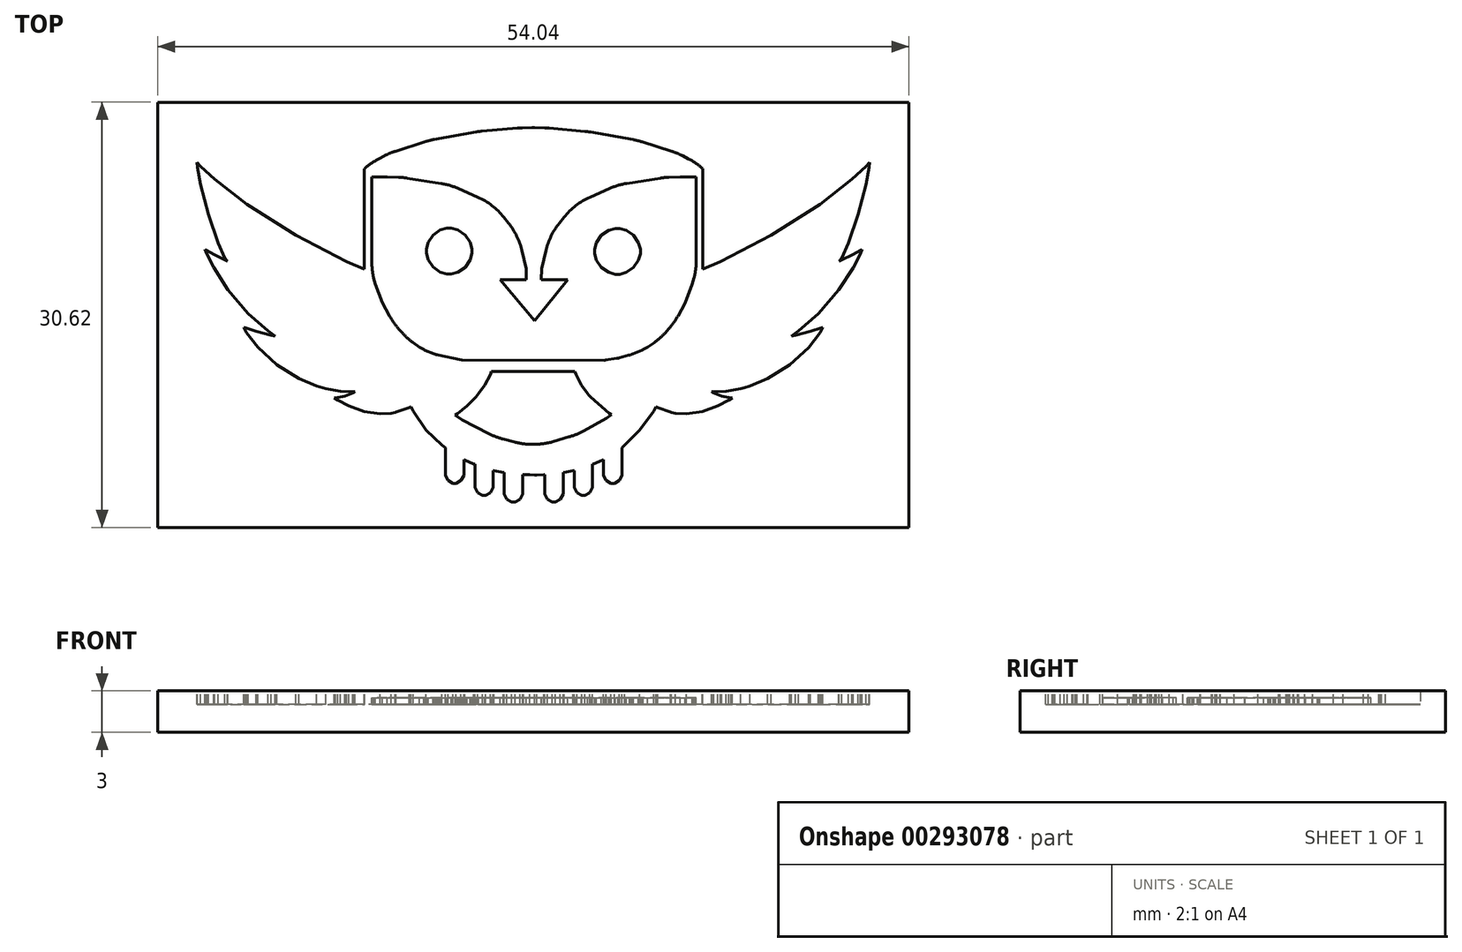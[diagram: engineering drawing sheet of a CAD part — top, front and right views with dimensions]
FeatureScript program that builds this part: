
annotation { "Feature Type Name" : "Feature", "Feature Type Description" : "" }
export const myFeature = defineFeature(function(context is Context, id is Id, definition is map)
    precondition{}
    {
        {
            var Q0;
            Q0=qCreatedBy(makeId("Top.planeOp"),FACE);
            var sketch = newSketch(context, id + "F0", { "sketchPlane" : qUnion([Q0])});
            skLineSegment(sketch, "E0.bottom", {"start": v(27.02, -15.3) * mm, "end": v(-27.02, -15.3) * mm});
            skLineSegment(sketch, "E0.top", {"start": v(27.02, 15.3) * mm, "end": v(-27.02, 15.3) * mm});
            skLineSegment(sketch, "E0.left", {"start": v(27.02, -15.3) * mm, "end": v(27.02, 15.3) * mm});
            skLineSegment(sketch, "E0.right", {"start": v(-27.02, -15.3) * mm, "end": v(-27.02, 15.3) * mm});
            skPoint(sketch, "E0.middle", {"position": v(0, 0) * mm});
            skSolve(sketch);
        }
        {
            var Q0;
            Q0 = qSketchRegion(id + "F0", true);
            extrude(context, id + "F1", {"entities" : qUnion([Q0]), "depth" : 3 * mm});
        }
        {
            var Q0;
            Q0=makeQuery(id+"F1.opExtrude","CAP_FACE",FACE,{"disambiguationData":[OSD([sQuery(id+"F0.wireOp",EDGE,"E0.bottom"),sQuery(id+"F0.wireOp",EDGE,"E0.top"),sQuery(id+"F0.wireOp",EDGE,"E0.left"),sQuery(id+"F0.wireOp",EDGE,"E0.right")])],"isStart":false});
            var sketch = newSketch(context, id + "F2", { "sketchPlane" : qUnion([Q0])});
            skLineSegment(sketch, "E1.bottom", {"start": v(35, -35) * mm, "end": v(-35, -35) * mm});
            skLineSegment(sketch, "E1.top", {"start": v(35, 35) * mm, "end": v(-35, 35) * mm});
            skLineSegment(sketch, "E1.left", {"start": v(35, -35) * mm, "end": v(35, 35) * mm});
            skLineSegment(sketch, "E1.right", {"start": v(-35, -35) * mm, "end": v(-35, 35) * mm});
            skPoint(sketch, "E1.middle", {"position": v(0, 0) * mm});
            skLineSegment(sketch, "E2", {"start": v(18.57, -1.52) * mm, "end": v(18.84, -1.46) * mm});
            skLineSegment(sketch, "E3", {"start": v(18.84, -1.46) * mm, "end": v(19.95, -1.17) * mm});
            skLineSegment(sketch, "E4", {"start": v(19.95, -1.17) * mm, "end": v(20.72, -0.93) * mm});
            skLineSegment(sketch, "E5", {"start": v(20.72, -0.93) * mm, "end": v(20.82, -0.89) * mm});
            skLineSegment(sketch, "E6", {"start": v(20.82, -0.89) * mm, "end": v(20.63, -1.28) * mm});
            skLineSegment(sketch, "E7", {"start": v(20.63, -1.28) * mm, "end": v(19.82, -2.35) * mm});
            skLineSegment(sketch, "E8", {"start": v(19.82, -2.35) * mm, "end": v(18.46, -3.6) * mm});
            skLineSegment(sketch, "E9", {"start": v(18.46, -3.6) * mm, "end": v(16.86, -4.6) * mm});
            skLineSegment(sketch, "E10", {"start": v(16.86, -4.6) * mm, "end": v(15.6, -5.13) * mm});
            skLineSegment(sketch, "E11", {"start": v(15.6, -5.13) * mm, "end": v(15.16, -5.25) * mm});
            skLineSegment(sketch, "E12", {"start": v(15.16, -5.25) * mm, "end": v(14.93, -5.32) * mm});
            skLineSegment(sketch, "E13", {"start": v(14.93, -5.32) * mm, "end": v(13.88, -5.5) * mm});
            skLineSegment(sketch, "E14", {"start": v(13.88, -5.5) * mm, "end": v(12.98, -5.55) * mm});
            skLineSegment(sketch, "E15", {"start": v(12.98, -5.55) * mm, "end": v(12.83, -5.54) * mm});
            skLineSegment(sketch, "E16", {"start": v(12.83, -5.54) * mm, "end": v(12.92, -5.6) * mm});
            skLineSegment(sketch, "E17", {"start": v(12.92, -5.6) * mm, "end": v(13.55, -5.85) * mm});
            skLineSegment(sketch, "E18", {"start": v(13.55, -5.85) * mm, "end": v(14.21, -5.99) * mm});
            skLineSegment(sketch, "E19", {"start": v(14.21, -5.99) * mm, "end": v(14.31, -6) * mm});
            skLineSegment(sketch, "E20", {"start": v(14.31, -6) * mm, "end": v(14.06, -6.15) * mm});
            skLineSegment(sketch, "E21", {"start": v(14.06, -6.15) * mm, "end": v(13.26, -6.56) * mm});
            skLineSegment(sketch, "E22", {"start": v(13.26, -6.56) * mm, "end": v(12.15, -6.97) * mm});
            skLineSegment(sketch, "E23", {"start": v(12.15, -6.97) * mm, "end": v(11.03, -7.14) * mm});
            skLineSegment(sketch, "E24", {"start": v(11.03, -7.14) * mm, "end": v(10.2, -7.1) * mm});
            skLineSegment(sketch, "E25", {"start": v(10.2, -7.1) * mm, "end": v(9.95, -7.02) * mm});
            skLineSegment(sketch, "E26", {"start": v(9.95, -7.02) * mm, "end": v(9.87, -7) * mm});
            skLineSegment(sketch, "E27", {"start": v(9.87, -7) * mm, "end": v(8.94, -6.67) * mm});
            skLineSegment(sketch, "E28", {"start": v(8.94, -6.67) * mm, "end": v(8.84, -6.63) * mm});
            skLineSegment(sketch, "E29", {"start": v(8.84, -6.63) * mm, "end": v(8.66, -6.94) * mm});
            skLineSegment(sketch, "E30", {"start": v(8.66, -6.94) * mm, "end": v(7.64, -8.3) * mm});
            skLineSegment(sketch, "E31", {"start": v(7.64, -8.3) * mm, "end": v(6.57, -9.39) * mm});
            skLineSegment(sketch, "E32", {"start": v(6.57, -9.39) * mm, "end": v(6.38, -9.56) * mm});
            skLineSegment(sketch, "E33", {"start": v(6.38, -9.56) * mm, "end": v(6.38, -11.44) * mm});
            skLineSegment(sketch, "E34", {"start": v(6.38, -11.44) * mm, "end": v(6.38, -11.56) * mm});
            skLineSegment(sketch, "E35", {"start": v(6.38, -11.56) * mm, "end": v(6.18, -11.93) * mm});
            skLineSegment(sketch, "E36", {"start": v(6.18, -11.93) * mm, "end": v(5.83, -12.13) * mm});
            skLineSegment(sketch, "E37", {"start": v(5.83, -12.13) * mm, "end": v(5.71, -12.13) * mm});
            skLineSegment(sketch, "E38", {"start": v(5.71, -12.13) * mm, "end": v(5.6, -12.13) * mm});
            skLineSegment(sketch, "E39", {"start": v(5.6, -12.13) * mm, "end": v(5.24, -11.93) * mm});
            skLineSegment(sketch, "E40", {"start": v(5.24, -11.93) * mm, "end": v(5.05, -11.56) * mm});
            skLineSegment(sketch, "E41", {"start": v(5.05, -11.56) * mm, "end": v(5.05, -11.44) * mm});
            skLineSegment(sketch, "E42", {"start": v(5.05, -11.44) * mm, "end": v(5.05, -10.44) * mm});
            skLineSegment(sketch, "E43", {"start": v(5.05, -10.44) * mm, "end": v(4.99, -10.46) * mm});
            skLineSegment(sketch, "E44", {"start": v(4.99, -10.46) * mm, "end": v(4.33, -10.73) * mm});
            skLineSegment(sketch, "E45", {"start": v(4.33, -10.73) * mm, "end": v(4.26, -10.75) * mm});
            skLineSegment(sketch, "E46", {"start": v(4.26, -10.75) * mm, "end": v(4.26, -12.32) * mm});
            skLineSegment(sketch, "E47", {"start": v(4.26, -12.32) * mm, "end": v(4.26, -12.44) * mm});
            skLineSegment(sketch, "E48", {"start": v(4.26, -12.44) * mm, "end": v(4.07, -12.8) * mm});
            skLineSegment(sketch, "E49", {"start": v(4.07, -12.8) * mm, "end": v(3.71, -13) * mm});
            skLineSegment(sketch, "E50", {"start": v(3.71, -13) * mm, "end": v(3.6, -13) * mm});
            skLineSegment(sketch, "E51", {"start": v(3.6, -13) * mm, "end": v(3.48, -13) * mm});
            skLineSegment(sketch, "E52", {"start": v(3.48, -13) * mm, "end": v(3.13, -12.8) * mm});
            skLineSegment(sketch, "E53", {"start": v(3.13, -12.8) * mm, "end": v(2.94, -12.44) * mm});
            skLineSegment(sketch, "E54", {"start": v(2.94, -12.44) * mm, "end": v(2.94, -12.32) * mm});
            skLineSegment(sketch, "E55", {"start": v(2.94, -12.32) * mm, "end": v(2.94, -11.2) * mm});
            skLineSegment(sketch, "E56", {"start": v(2.94, -11.2) * mm, "end": v(2.87, -11.22) * mm});
            skLineSegment(sketch, "E57", {"start": v(2.87, -11.22) * mm, "end": v(2.2, -11.33) * mm});
            skLineSegment(sketch, "E58", {"start": v(2.2, -11.33) * mm, "end": v(2.14, -11.34) * mm});
            skLineSegment(sketch, "E59", {"start": v(2.14, -11.34) * mm, "end": v(2.14, -12.8) * mm});
            skLineSegment(sketch, "E60", {"start": v(2.14, -12.8) * mm, "end": v(2.14, -12.91) * mm});
            skLineSegment(sketch, "E61", {"start": v(2.14, -12.91) * mm, "end": v(1.95, -13.28) * mm});
            skLineSegment(sketch, "E62", {"start": v(1.95, -13.28) * mm, "end": v(1.6, -13.48) * mm});
            skLineSegment(sketch, "E63", {"start": v(1.6, -13.48) * mm, "end": v(1.48, -13.48) * mm});
            skLineSegment(sketch, "E64", {"start": v(1.48, -13.48) * mm, "end": v(1.36, -13.48) * mm});
            skLineSegment(sketch, "E65", {"start": v(1.36, -13.48) * mm, "end": v(1.01, -13.28) * mm});
            skLineSegment(sketch, "E66", {"start": v(1.01, -13.28) * mm, "end": v(0.82, -12.91) * mm});
            skLineSegment(sketch, "E67", {"start": v(0.82, -12.91) * mm, "end": v(0.82, -12.8) * mm});
            skLineSegment(sketch, "E68", {"start": v(0.82, -12.8) * mm, "end": v(0.82, -11.5) * mm});
            skLineSegment(sketch, "E69", {"start": v(0.82, -11.5) * mm, "end": v(0.75, -11.5) * mm});
            skLineSegment(sketch, "E70", {"start": v(0.75, -11.5) * mm, "end": v(0.25, -11.52) * mm});
            skLineSegment(sketch, "E71", {"start": v(0.25, -11.52) * mm, "end": v(0.08, -11.52) * mm});
            skLineSegment(sketch, "E72", {"start": v(0.08, -11.52) * mm, "end": v(-0.25, -11.52) * mm});
            skLineSegment(sketch, "E73", {"start": v(-0.25, -11.52) * mm, "end": v(-0.7, -11.5) * mm});
            skLineSegment(sketch, "E74", {"start": v(-0.7, -11.5) * mm, "end": v(-0.77, -11.5) * mm});
            skLineSegment(sketch, "E75", {"start": v(-0.77, -11.5) * mm, "end": v(-0.77, -12.8) * mm});
            skLineSegment(sketch, "E76", {"start": v(-0.77, -12.8) * mm, "end": v(-0.77, -12.91) * mm});
            skLineSegment(sketch, "E77", {"start": v(-0.77, -12.91) * mm, "end": v(-0.96, -13.28) * mm});
            skLineSegment(sketch, "E78", {"start": v(-0.96, -13.28) * mm, "end": v(-1.31, -13.48) * mm});
            skLineSegment(sketch, "E79", {"start": v(-1.31, -13.48) * mm, "end": v(-1.43, -13.48) * mm});
            skLineSegment(sketch, "E80", {"start": v(-1.43, -13.48) * mm, "end": v(-1.55, -13.48) * mm});
            skLineSegment(sketch, "E81", {"start": v(-1.55, -13.48) * mm, "end": v(-1.9, -13.28) * mm});
            skLineSegment(sketch, "E82", {"start": v(-1.9, -13.28) * mm, "end": v(-2.1, -12.91) * mm});
            skLineSegment(sketch, "E83", {"start": v(-2.1, -12.91) * mm, "end": v(-2.1, -12.8) * mm});
            skLineSegment(sketch, "E84", {"start": v(-2.1, -12.8) * mm, "end": v(-2.1, -11.34) * mm});
            skLineSegment(sketch, "E85", {"start": v(-2.1, -11.34) * mm, "end": v(-2.16, -11.33) * mm});
            skLineSegment(sketch, "E86", {"start": v(-2.16, -11.33) * mm, "end": v(-2.82, -11.22) * mm});
            skLineSegment(sketch, "E87", {"start": v(-2.82, -11.22) * mm, "end": v(-2.88, -11.2) * mm});
            skLineSegment(sketch, "E88", {"start": v(-2.88, -11.2) * mm, "end": v(-2.88, -12.32) * mm});
            skLineSegment(sketch, "E89", {"start": v(-2.88, -12.32) * mm, "end": v(-2.88, -12.44) * mm});
            skLineSegment(sketch, "E90", {"start": v(-2.88, -12.44) * mm, "end": v(-3.08, -12.8) * mm});
            skLineSegment(sketch, "E91", {"start": v(-3.08, -12.8) * mm, "end": v(-3.43, -13) * mm});
            skLineSegment(sketch, "E92", {"start": v(-3.43, -13) * mm, "end": v(-3.55, -13) * mm});
            skLineSegment(sketch, "E93", {"start": v(-3.55, -13) * mm, "end": v(-3.66, -13) * mm});
            skLineSegment(sketch, "E94", {"start": v(-3.66, -13) * mm, "end": v(-4.02, -12.8) * mm});
            skLineSegment(sketch, "E95", {"start": v(-4.02, -12.8) * mm, "end": v(-4.2, -12.44) * mm});
            skLineSegment(sketch, "E96", {"start": v(-4.2, -12.44) * mm, "end": v(-4.2, -12.32) * mm});
            skLineSegment(sketch, "E97", {"start": v(-4.2, -12.32) * mm, "end": v(-4.2, -10.75) * mm});
            skLineSegment(sketch, "E98", {"start": v(-4.2, -10.75) * mm, "end": v(-4.27, -10.73) * mm});
            skLineSegment(sketch, "E99", {"start": v(-4.27, -10.73) * mm, "end": v(-4.93, -10.47) * mm});
            skLineSegment(sketch, "E100", {"start": v(-4.93, -10.47) * mm, "end": v(-5, -10.44) * mm});
            skLineSegment(sketch, "E101", {"start": v(-5, -10.44) * mm, "end": v(-5, -11.44) * mm});
            skLineSegment(sketch, "E102", {"start": v(-5, -11.44) * mm, "end": v(-5, -11.56) * mm});
            skLineSegment(sketch, "E103", {"start": v(-5, -11.56) * mm, "end": v(-5.2, -11.93) * mm});
            skLineSegment(sketch, "E104", {"start": v(-5.2, -11.93) * mm, "end": v(-5.55, -12.13) * mm});
            skLineSegment(sketch, "E105", {"start": v(-5.55, -12.13) * mm, "end": v(-5.66, -12.13) * mm});
            skLineSegment(sketch, "E106", {"start": v(-5.66, -12.13) * mm, "end": v(-5.78, -12.13) * mm});
            skLineSegment(sketch, "E107", {"start": v(-5.78, -12.13) * mm, "end": v(-6.13, -11.93) * mm});
            skLineSegment(sketch, "E108", {"start": v(-6.13, -11.93) * mm, "end": v(-6.32, -11.56) * mm});
            skLineSegment(sketch, "E109", {"start": v(-6.32, -11.56) * mm, "end": v(-6.32, -11.44) * mm});
            skLineSegment(sketch, "E110", {"start": v(-6.32, -11.44) * mm, "end": v(-6.32, -9.56) * mm});
            skLineSegment(sketch, "E111", {"start": v(-6.32, -9.56) * mm, "end": v(-6.59, -9.39) * mm});
            skLineSegment(sketch, "E112", {"start": v(-6.59, -9.39) * mm, "end": v(-7.7, -8.3) * mm});
            skLineSegment(sketch, "E113", {"start": v(-7.7, -8.3) * mm, "end": v(-8.64, -6.94) * mm});
            skLineSegment(sketch, "E114", {"start": v(-8.64, -6.94) * mm, "end": v(-8.81, -6.63) * mm});
            skLineSegment(sketch, "E115", {"start": v(-8.81, -6.63) * mm, "end": v(-8.92, -6.67) * mm});
            skLineSegment(sketch, "E116", {"start": v(-8.92, -6.67) * mm, "end": v(-9.88, -7) * mm});
            skLineSegment(sketch, "E117", {"start": v(-9.88, -7) * mm, "end": v(-9.95, -7.02) * mm});
            skLineSegment(sketch, "E118", {"start": v(-9.95, -7.02) * mm, "end": v(-10.2, -7.1) * mm});
            skLineSegment(sketch, "E119", {"start": v(-10.2, -7.1) * mm, "end": v(-11.03, -7.14) * mm});
            skLineSegment(sketch, "E120", {"start": v(-11.03, -7.14) * mm, "end": v(-12.15, -6.97) * mm});
            skLineSegment(sketch, "E121", {"start": v(-12.15, -6.97) * mm, "end": v(-13.26, -6.56) * mm});
            skLineSegment(sketch, "E122", {"start": v(-13.26, -6.56) * mm, "end": v(-14.06, -6.15) * mm});
            skLineSegment(sketch, "E123", {"start": v(-14.06, -6.15) * mm, "end": v(-14.31, -6) * mm});
            skLineSegment(sketch, "E124", {"start": v(-14.31, -6) * mm, "end": v(-14.21, -5.99) * mm});
            skLineSegment(sketch, "E125", {"start": v(-14.21, -5.99) * mm, "end": v(-13.55, -5.85) * mm});
            skLineSegment(sketch, "E126", {"start": v(-13.55, -5.85) * mm, "end": v(-12.92, -5.6) * mm});
            skLineSegment(sketch, "E127", {"start": v(-12.92, -5.6) * mm, "end": v(-12.83, -5.54) * mm});
            skLineSegment(sketch, "E128", {"start": v(-12.83, -5.54) * mm, "end": v(-12.99, -5.55) * mm});
            skLineSegment(sketch, "E129", {"start": v(-12.99, -5.55) * mm, "end": v(-13.88, -5.5) * mm});
            skLineSegment(sketch, "E130", {"start": v(-13.88, -5.5) * mm, "end": v(-14.93, -5.32) * mm});
            skLineSegment(sketch, "E131", {"start": v(-14.93, -5.32) * mm, "end": v(-15.16, -5.25) * mm});
            skLineSegment(sketch, "E132", {"start": v(-15.16, -5.25) * mm, "end": v(-15.6, -5.13) * mm});
            skLineSegment(sketch, "E133", {"start": v(-15.6, -5.13) * mm, "end": v(-16.86, -4.59) * mm});
            skLineSegment(sketch, "E134", {"start": v(-16.86, -4.59) * mm, "end": v(-18.46, -3.6) * mm});
            skLineSegment(sketch, "E135", {"start": v(-18.46, -3.6) * mm, "end": v(-19.82, -2.34) * mm});
            skLineSegment(sketch, "E136", {"start": v(-19.82, -2.34) * mm, "end": v(-20.63, -1.28) * mm});
            skLineSegment(sketch, "E137", {"start": v(-20.63, -1.28) * mm, "end": v(-20.82, -0.89) * mm});
            skLineSegment(sketch, "E138", {"start": v(-20.82, -0.89) * mm, "end": v(-20.72, -0.93) * mm});
            skLineSegment(sketch, "E139", {"start": v(-20.72, -0.93) * mm, "end": v(-19.95, -1.17) * mm});
            skLineSegment(sketch, "E140", {"start": v(-19.95, -1.17) * mm, "end": v(-18.85, -1.46) * mm});
            skLineSegment(sketch, "E141", {"start": v(-18.85, -1.46) * mm, "end": v(-18.57, -1.52) * mm});
            skLineSegment(sketch, "E142", {"start": v(-18.57, -1.52) * mm, "end": v(-19.1, -1.17) * mm});
            skLineSegment(sketch, "E143", {"start": v(-19.1, -1.17) * mm, "end": v(-20.52, 0.1) * mm});
            skLineSegment(sketch, "E144", {"start": v(-20.52, 0.1) * mm, "end": v(-21.97, 1.8) * mm});
            skLineSegment(sketch, "E145", {"start": v(-21.97, 1.8) * mm, "end": v(-23, 3.4) * mm});
            skLineSegment(sketch, "E146", {"start": v(-23, 3.4) * mm, "end": v(-23.5, 4.39) * mm});
            skLineSegment(sketch, "E147", {"start": v(-23.5, 4.39) * mm, "end": v(-23.63, 4.72) * mm});
            skLineSegment(sketch, "E148", {"start": v(-23.63, 4.72) * mm, "end": v(-23.54, 4.67) * mm});
            skLineSegment(sketch, "E149", {"start": v(-23.54, 4.67) * mm, "end": v(-22.97, 4.35) * mm});
            skLineSegment(sketch, "E150", {"start": v(-22.97, 4.35) * mm, "end": v(-22.2, 3.96) * mm});
            skLineSegment(sketch, "E151", {"start": v(-22.2, 3.96) * mm, "end": v(-22.01, 3.88) * mm});
            skLineSegment(sketch, "E152", {"start": v(-22.01, 3.88) * mm, "end": v(-22.2, 4.1) * mm});
            skLineSegment(sketch, "E153", {"start": v(-22.2, 4.1) * mm, "end": v(-22.67, 5.16) * mm});
            skLineSegment(sketch, "E154", {"start": v(-22.67, 5.16) * mm, "end": v(-23.38, 7.22) * mm});
            skLineSegment(sketch, "E155", {"start": v(-23.38, 7.22) * mm, "end": v(-23.94, 9.4) * mm});
            skLineSegment(sketch, "E156", {"start": v(-23.94, 9.4) * mm, "end": v(-24.18, 10.62) * mm});
            skLineSegment(sketch, "E157", {"start": v(-24.18, 10.62) * mm, "end": v(-24.18, 10.97) * mm});
            skLineSegment(sketch, "E158", {"start": v(-24.18, 10.97) * mm, "end": v(-23.93, 10.68) * mm});
            skLineSegment(sketch, "E159", {"start": v(-23.93, 10.68) * mm, "end": v(-22.93, 9.75) * mm});
            skLineSegment(sketch, "E160", {"start": v(-22.93, 9.75) * mm, "end": v(-20.62, 7.95) * mm});
            skLineSegment(sketch, "E161", {"start": v(-20.62, 7.95) * mm, "end": v(-17.09, 5.73) * mm});
            skLineSegment(sketch, "E162", {"start": v(-17.09, 5.73) * mm, "end": v(-13.42, 3.84) * mm});
            skLineSegment(sketch, "E163", {"start": v(-13.42, 3.84) * mm, "end": v(-12.17, 3.3) * mm});
            skLineSegment(sketch, "E164", {"start": v(-12.17, 3.3) * mm, "end": v(-12.17, 10.5) * mm});
            skLineSegment(sketch, "E165", {"start": v(-12.17, 10.5) * mm, "end": v(-12.14, 10.5) * mm});
            skLineSegment(sketch, "E166", {"start": v(-12.14, 10.5) * mm, "end": v(-12.14, 10.52) * mm});
            skLineSegment(sketch, "E167", {"start": v(-12.14, 10.52) * mm, "end": v(-11.78, 10.89) * mm});
            skLineSegment(sketch, "E168", {"start": v(-11.78, 10.89) * mm, "end": v(-10.33, 11.65) * mm});
            skLineSegment(sketch, "E169", {"start": v(-10.33, 11.65) * mm, "end": v(-7.47, 12.57) * mm});
            skLineSegment(sketch, "E170", {"start": v(-7.47, 12.57) * mm, "end": v(-3.92, 13.2) * mm});
            skLineSegment(sketch, "E171", {"start": v(-3.92, 13.2) * mm, "end": v(-0.98, 13.46) * mm});
            skLineSegment(sketch, "E172", {"start": v(-0.98, 13.46) * mm, "end": v(0, 13.48) * mm});
            skLineSegment(sketch, "E173", {"start": v(0, 13.48) * mm, "end": v(0.98, 13.46) * mm});
            skLineSegment(sketch, "E174", {"start": v(0.98, 13.46) * mm, "end": v(3.92, 13.19) * mm});
            skLineSegment(sketch, "E175", {"start": v(3.92, 13.19) * mm, "end": v(7.5, 12.55) * mm});
            skLineSegment(sketch, "E176", {"start": v(7.5, 12.55) * mm, "end": v(10.37, 11.64) * mm});
            skLineSegment(sketch, "E177", {"start": v(10.37, 11.64) * mm, "end": v(11.83, 10.89) * mm});
            skLineSegment(sketch, "E178", {"start": v(11.83, 10.89) * mm, "end": v(12.2, 10.52) * mm});
            skLineSegment(sketch, "E179", {"start": v(12.2, 10.52) * mm, "end": v(12.2, 10.46) * mm});
            skLineSegment(sketch, "E180", {"start": v(12.2, 10.46) * mm, "end": v(12.17, 10.46) * mm});
            skLineSegment(sketch, "E181", {"start": v(12.17, 10.46) * mm, "end": v(12.2, 10.46) * mm});
            skLineSegment(sketch, "E182", {"start": v(12.2, 10.46) * mm, "end": v(12.2, 3.3) * mm});
            skLineSegment(sketch, "E183", {"start": v(12.2, 3.3) * mm, "end": v(13.45, 3.84) * mm});
            skLineSegment(sketch, "E184", {"start": v(13.45, 3.84) * mm, "end": v(17.1, 5.73) * mm});
            skLineSegment(sketch, "E185", {"start": v(17.1, 5.73) * mm, "end": v(20.63, 7.95) * mm});
            skLineSegment(sketch, "E186", {"start": v(20.63, 7.95) * mm, "end": v(22.93, 9.75) * mm});
            skLineSegment(sketch, "E187", {"start": v(22.93, 9.75) * mm, "end": v(23.92, 10.68) * mm});
            skLineSegment(sketch, "E188", {"start": v(23.92, 10.68) * mm, "end": v(24.18, 10.97) * mm});
            skLineSegment(sketch, "E189", {"start": v(24.18, 10.97) * mm, "end": v(24.18, 10.62) * mm});
            skLineSegment(sketch, "E190", {"start": v(24.18, 10.62) * mm, "end": v(23.94, 9.4) * mm});
            skLineSegment(sketch, "E191", {"start": v(23.94, 9.4) * mm, "end": v(23.37, 7.23) * mm});
            skLineSegment(sketch, "E192", {"start": v(23.37, 7.23) * mm, "end": v(22.67, 5.16) * mm});
            skLineSegment(sketch, "E193", {"start": v(22.67, 5.16) * mm, "end": v(22.2, 4.1) * mm});
            skLineSegment(sketch, "E194", {"start": v(22.2, 4.1) * mm, "end": v(22.01, 3.88) * mm});
            skLineSegment(sketch, "E195", {"start": v(22.01, 3.88) * mm, "end": v(22.2, 3.96) * mm});
            skLineSegment(sketch, "E196", {"start": v(22.2, 3.96) * mm, "end": v(22.98, 4.35) * mm});
            skLineSegment(sketch, "E197", {"start": v(22.98, 4.35) * mm, "end": v(23.57, 4.67) * mm});
            skLineSegment(sketch, "E198", {"start": v(23.57, 4.67) * mm, "end": v(23.65, 4.72) * mm});
            skLineSegment(sketch, "E199", {"start": v(23.65, 4.72) * mm, "end": v(23.51, 4.38) * mm});
            skLineSegment(sketch, "E200", {"start": v(23.51, 4.38) * mm, "end": v(23, 3.4) * mm});
            skLineSegment(sketch, "E201", {"start": v(23, 3.4) * mm, "end": v(21.98, 1.79) * mm});
            skLineSegment(sketch, "E202", {"start": v(21.98, 1.79) * mm, "end": v(20.52, 0.1) * mm});
            skLineSegment(sketch, "E203", {"start": v(20.52, 0.1) * mm, "end": v(19.1, -1.17) * mm});
            skLineSegment(sketch, "E204", {"start": v(19.1, -1.17) * mm, "end": v(18.57, -1.52) * mm});
            skLineSegment(sketch, "E205", {"start": v(5.1, -3.27) * mm, "end": v(5.2, -3.25) * mm});
            skLineSegment(sketch, "E206", {"start": v(5.2, -3.25) * mm, "end": v(6.01, -3.12) * mm});
            skLineSegment(sketch, "E207", {"start": v(6.01, -3.12) * mm, "end": v(6.09, -3.1) * mm});
            skLineSegment(sketch, "E208", {"start": v(6.09, -3.1) * mm, "end": v(6.1, -3.1) * mm});
            skLineSegment(sketch, "E209", {"start": v(6.1, -3.1) * mm, "end": v(6.11, -3.1) * mm});
            skLineSegment(sketch, "E210", {"start": v(6.11, -3.1) * mm, "end": v(6.18, -3.1) * mm});
            skLineSegment(sketch, "E211", {"start": v(6.18, -3.1) * mm, "end": v(6.86, -2.92) * mm});
            skLineSegment(sketch, "E212", {"start": v(6.86, -2.92) * mm, "end": v(6.93, -2.9) * mm});
            skLineSegment(sketch, "E213", {"start": v(6.93, -2.9) * mm, "end": v(6.96, -2.9) * mm});
            skLineSegment(sketch, "E214", {"start": v(6.96, -2.9) * mm, "end": v(6.97, -2.9) * mm});
            skLineSegment(sketch, "E215", {"start": v(6.97, -2.9) * mm, "end": v(7.08, -2.85) * mm});
            skLineSegment(sketch, "E216", {"start": v(7.08, -2.85) * mm, "end": v(7.09, -2.85) * mm});
            skLineSegment(sketch, "E217", {"start": v(7.09, -2.85) * mm, "end": v(7.16, -2.82) * mm});
            skLineSegment(sketch, "E218", {"start": v(7.16, -2.82) * mm, "end": v(7.8, -2.55) * mm});
            skLineSegment(sketch, "E219", {"start": v(7.8, -2.55) * mm, "end": v(7.86, -2.53) * mm});
            skLineSegment(sketch, "E220", {"start": v(7.86, -2.53) * mm, "end": v(7.9, -2.5) * mm});
            skLineSegment(sketch, "E221", {"start": v(7.9, -2.5) * mm, "end": v(7.91, -2.5) * mm});
            skLineSegment(sketch, "E222", {"start": v(7.91, -2.5) * mm, "end": v(8.23, -2.34) * mm});
            skLineSegment(sketch, "E223", {"start": v(8.23, -2.34) * mm, "end": v(9.12, -1.7) * mm});
            skLineSegment(sketch, "E224", {"start": v(9.12, -1.7) * mm, "end": v(10.12, -0.59) * mm});
            skLineSegment(sketch, "E225", {"start": v(10.12, -0.59) * mm, "end": v(10.93, 0.86) * mm});
            skLineSegment(sketch, "E226", {"start": v(10.93, 0.86) * mm, "end": v(11.43, 2.2) * mm});
            skLineSegment(sketch, "E227", {"start": v(11.43, 2.2) * mm, "end": v(11.56, 2.66) * mm});
            skLineSegment(sketch, "E228", {"start": v(11.56, 2.66) * mm, "end": v(11.57, 2.71) * mm});
            skLineSegment(sketch, "E229", {"start": v(11.57, 2.71) * mm, "end": v(11.72, 3.1) * mm});
            skLineSegment(sketch, "E230", {"start": v(11.72, 3.1) * mm, "end": v(11.72, 3.24) * mm});
            skLineSegment(sketch, "E231", {"start": v(11.72, 3.24) * mm, "end": v(11.72, 9.93) * mm});
            skLineSegment(sketch, "E232", {"start": v(11.72, 9.93) * mm, "end": v(10.58, 9.93) * mm});
            skLineSegment(sketch, "E233", {"start": v(10.58, 9.93) * mm, "end": v(9.45, 9.9) * mm});
            skLineSegment(sketch, "E234", {"start": v(9.45, 9.9) * mm, "end": v(6.08, 9.36) * mm});
            skLineSegment(sketch, "E235", {"start": v(6.08, 9.36) * mm, "end": v(2.97, 7.98) * mm});
            skLineSegment(sketch, "E236", {"start": v(2.97, 7.98) * mm, "end": v(1.17, 5.72) * mm});
            skLineSegment(sketch, "E237", {"start": v(1.17, 5.72) * mm, "end": v(0.59, 3.33) * mm});
            skLineSegment(sketch, "E238", {"start": v(0.59, 3.33) * mm, "end": v(0.58, 2.53) * mm});
            skLineSegment(sketch, "E239", {"start": v(0.58, 2.53) * mm, "end": v(2.46, 2.53) * mm});
            skLineSegment(sketch, "E240", {"start": v(2.46, 2.53) * mm, "end": v(0.08, -0.41) * mm});
            skLineSegment(sketch, "E241", {"start": v(0.08, -0.41) * mm, "end": v(-2.38, 2.53) * mm});
            skLineSegment(sketch, "E242", {"start": v(-2.38, 2.53) * mm, "end": v(-0.5, 2.53) * mm});
            skLineSegment(sketch, "E243", {"start": v(-0.5, 2.53) * mm, "end": v(-0.5, 3.33) * mm});
            skLineSegment(sketch, "E244", {"start": v(-0.5, 3.33) * mm, "end": v(-1.08, 5.72) * mm});
            skLineSegment(sketch, "E245", {"start": v(-1.08, 5.72) * mm, "end": v(-2.89, 7.98) * mm});
            skLineSegment(sketch, "E246", {"start": v(-2.89, 7.98) * mm, "end": v(-6, 9.36) * mm});
            skLineSegment(sketch, "E247", {"start": v(-6, 9.36) * mm, "end": v(-9.37, 9.9) * mm});
            skLineSegment(sketch, "E248", {"start": v(-9.37, 9.9) * mm, "end": v(-10.5, 9.93) * mm});
            skLineSegment(sketch, "E249", {"start": v(-10.5, 9.93) * mm, "end": v(-11.62, 9.93) * mm});
            skLineSegment(sketch, "E250", {"start": v(-11.62, 9.93) * mm, "end": v(-11.62, 3.24) * mm});
            skLineSegment(sketch, "E251", {"start": v(-11.62, 3.24) * mm, "end": v(-11.62, 3.1) * mm});
            skLineSegment(sketch, "E252", {"start": v(-11.62, 3.1) * mm, "end": v(-11.5, 2.71) * mm});
            skLineSegment(sketch, "E253", {"start": v(-11.5, 2.71) * mm, "end": v(-11.48, 2.66) * mm});
            skLineSegment(sketch, "E254", {"start": v(-11.48, 2.66) * mm, "end": v(-11.36, 2.2) * mm});
            skLineSegment(sketch, "E255", {"start": v(-11.36, 2.2) * mm, "end": v(-10.87, 0.87) * mm});
            skLineSegment(sketch, "E256", {"start": v(-10.87, 0.87) * mm, "end": v(-10.07, -0.57) * mm});
            skLineSegment(sketch, "E257", {"start": v(-10.07, -0.57) * mm, "end": v(-9.08, -1.68) * mm});
            skLineSegment(sketch, "E258", {"start": v(-9.08, -1.68) * mm, "end": v(-8.2, -2.34) * mm});
            skLineSegment(sketch, "E259", {"start": v(-8.2, -2.34) * mm, "end": v(-7.89, -2.5) * mm});
            skLineSegment(sketch, "E260", {"start": v(-7.89, -2.5) * mm, "end": v(-7.88, -2.5) * mm});
            skLineSegment(sketch, "E261", {"start": v(-7.88, -2.5) * mm, "end": v(-7.86, -2.52) * mm});
            skLineSegment(sketch, "E262", {"start": v(-7.86, -2.52) * mm, "end": v(-7.86, -2.53) * mm});
            skLineSegment(sketch, "E263", {"start": v(-7.86, -2.53) * mm, "end": v(-7.8, -2.55) * mm});
            skLineSegment(sketch, "E264", {"start": v(-7.8, -2.55) * mm, "end": v(-7.15, -2.82) * mm});
            skLineSegment(sketch, "E265", {"start": v(-7.15, -2.82) * mm, "end": v(-7.07, -2.85) * mm});
            skLineSegment(sketch, "E266", {"start": v(-7.07, -2.85) * mm, "end": v(-7.04, -2.85) * mm});
            skLineSegment(sketch, "E267", {"start": v(-7.04, -2.85) * mm, "end": v(-6.98, -2.87) * mm});
            skLineSegment(sketch, "E268", {"start": v(-6.98, -2.87) * mm, "end": v(-6.96, -2.87) * mm});
            skLineSegment(sketch, "E269", {"start": v(-6.96, -2.87) * mm, "end": v(-6.93, -2.87) * mm});
            skLineSegment(sketch, "E270", {"start": v(-6.93, -2.87) * mm, "end": v(-6.8, -2.92) * mm});
            skLineSegment(sketch, "E271", {"start": v(-6.8, -2.92) * mm, "end": v(-5.3, -3.22) * mm});
            skLineSegment(sketch, "E272", {"start": v(-5.3, -3.22) * mm, "end": v(-5.13, -3.24) * mm});
            skLineSegment(sketch, "E273", {"start": v(-5.13, -3.24) * mm, "end": v(5.1, -3.27) * mm});
            skLineSegment(sketch, "E274", {"start": v(-5.64, -7.21) * mm, "end": v(-5.13, -7.57) * mm});
            skLineSegment(sketch, "E275", {"start": v(-5.13, -7.57) * mm, "end": v(-2.72, -8.8) * mm});
            skLineSegment(sketch, "E276", {"start": v(-2.72, -8.8) * mm, "end": v(-0.72, -9.33) * mm});
            skLineSegment(sketch, "E277", {"start": v(-0.72, -9.33) * mm, "end": v(-0.05, -9.33) * mm});
            skLineSegment(sketch, "E278", {"start": v(-0.05, -9.33) * mm, "end": v(0.74, -9.33) * mm});
            skLineSegment(sketch, "E279", {"start": v(0.74, -9.33) * mm, "end": v(3.11, -8.63) * mm});
            skLineSegment(sketch, "E280", {"start": v(3.11, -8.63) * mm, "end": v(5.26, -7.43) * mm});
            skLineSegment(sketch, "E281", {"start": v(5.26, -7.43) * mm, "end": v(5.6, -7.18) * mm});
            skLineSegment(sketch, "E282", {"start": v(5.6, -7.18) * mm, "end": v(5.46, -7.1) * mm});
            skLineSegment(sketch, "E283", {"start": v(5.46, -7.1) * mm, "end": v(4.11, -5.93) * mm});
            skLineSegment(sketch, "E284", {"start": v(4.11, -5.93) * mm, "end": v(4, -5.78) * mm});
            skLineSegment(sketch, "E285", {"start": v(4, -5.78) * mm, "end": v(3.9, -5.67) * mm});
            skLineSegment(sketch, "E286", {"start": v(3.9, -5.67) * mm, "end": v(3.47, -5.06) * mm});
            skLineSegment(sketch, "E287", {"start": v(3.47, -5.06) * mm, "end": v(3.07, -4.29) * mm});
            skLineSegment(sketch, "E288", {"start": v(3.07, -4.29) * mm, "end": v(2.99, -4.09) * mm});
            skLineSegment(sketch, "E289", {"start": v(2.99, -4.09) * mm, "end": v(-3.02, -4.09) * mm});
            skLineSegment(sketch, "E290", {"start": v(-3.02, -4.09) * mm, "end": v(-3.1, -4.29) * mm});
            skLineSegment(sketch, "E291", {"start": v(-3.1, -4.29) * mm, "end": v(-3.5, -5.06) * mm});
            skLineSegment(sketch, "E292", {"start": v(-3.5, -5.06) * mm, "end": v(-3.93, -5.67) * mm});
            skLineSegment(sketch, "E293", {"start": v(-3.93, -5.67) * mm, "end": v(-4.02, -5.78) * mm});
            skLineSegment(sketch, "E294", {"start": v(-4.02, -5.78) * mm, "end": v(-4.14, -5.92) * mm});
            skLineSegment(sketch, "E295", {"start": v(-4.14, -5.92) * mm, "end": v(-4.76, -6.56) * mm});
            skLineSegment(sketch, "E296", {"start": v(-4.76, -6.56) * mm, "end": v(-5.48, -7.12) * mm});
            skLineSegment(sketch, "E297", {"start": v(-5.48, -7.12) * mm, "end": v(-5.64, -7.21) * mm});
            skLineSegment(sketch, "E298", {"start": v(-4.42, 4.6) * mm, "end": v(-4.42, 4.75) * mm});
            skLineSegment(sketch, "E299", {"start": v(-4.42, 4.75) * mm, "end": v(-4.55, 5.23) * mm});
            skLineSegment(sketch, "E300", {"start": v(-4.55, 5.23) * mm, "end": v(-4.9, 5.75) * mm});
            skLineSegment(sketch, "E301", {"start": v(-4.9, 5.75) * mm, "end": v(-5.42, 6.1) * mm});
            skLineSegment(sketch, "E302", {"start": v(-5.42, 6.1) * mm, "end": v(-5.9, 6.23) * mm});
            skLineSegment(sketch, "E303", {"start": v(-5.9, 6.23) * mm, "end": v(-6.06, 6.23) * mm});
            skLineSegment(sketch, "E304", {"start": v(-6.06, 6.23) * mm, "end": v(-6.22, 6.23) * mm});
            skLineSegment(sketch, "E305", {"start": v(-6.22, 6.23) * mm, "end": v(-6.7, 6.1) * mm});
            skLineSegment(sketch, "E306", {"start": v(-6.7, 6.1) * mm, "end": v(-7.22, 5.75) * mm});
            skLineSegment(sketch, "E307", {"start": v(-7.22, 5.75) * mm, "end": v(-7.57, 5.23) * mm});
            skLineSegment(sketch, "E308", {"start": v(-7.57, 5.23) * mm, "end": v(-7.7, 4.75) * mm});
            skLineSegment(sketch, "E309", {"start": v(-7.7, 4.75) * mm, "end": v(-7.7, 4.6) * mm});
            skLineSegment(sketch, "E310", {"start": v(-7.7, 4.6) * mm, "end": v(-7.7, 4.43) * mm});
            skLineSegment(sketch, "E311", {"start": v(-7.7, 4.43) * mm, "end": v(-7.57, 3.96) * mm});
            skLineSegment(sketch, "E312", {"start": v(-7.57, 3.96) * mm, "end": v(-7.22, 3.43) * mm});
            skLineSegment(sketch, "E313", {"start": v(-7.22, 3.43) * mm, "end": v(-6.7, 3.08) * mm});
            skLineSegment(sketch, "E314", {"start": v(-6.7, 3.08) * mm, "end": v(-6.22, 2.95) * mm});
            skLineSegment(sketch, "E315", {"start": v(-6.22, 2.95) * mm, "end": v(-6.06, 2.95) * mm});
            skLineSegment(sketch, "E316", {"start": v(-6.06, 2.95) * mm, "end": v(-5.9, 2.95) * mm});
            skLineSegment(sketch, "E317", {"start": v(-5.9, 2.95) * mm, "end": v(-5.42, 3.08) * mm});
            skLineSegment(sketch, "E318", {"start": v(-5.42, 3.08) * mm, "end": v(-4.9, 3.42) * mm});
            skLineSegment(sketch, "E319", {"start": v(-4.9, 3.42) * mm, "end": v(-4.55, 3.94) * mm});
            skLineSegment(sketch, "E320", {"start": v(-4.55, 3.94) * mm, "end": v(-4.42, 4.43) * mm});
            skLineSegment(sketch, "E321", {"start": v(-4.42, 4.43) * mm, "end": v(-4.42, 4.6) * mm});
            skLineSegment(sketch, "E322", {"start": v(6.06, 2.92) * mm, "end": v(6.22, 2.92) * mm});
            skLineSegment(sketch, "E323", {"start": v(6.22, 2.92) * mm, "end": v(6.7, 3.05) * mm});
            skLineSegment(sketch, "E324", {"start": v(6.7, 3.05) * mm, "end": v(7.22, 3.4) * mm});
            skLineSegment(sketch, "E325", {"start": v(7.22, 3.4) * mm, "end": v(7.57, 3.93) * mm});
            skLineSegment(sketch, "E326", {"start": v(7.57, 3.93) * mm, "end": v(7.7, 4.4) * mm});
            skLineSegment(sketch, "E327", {"start": v(7.7, 4.4) * mm, "end": v(7.7, 4.56) * mm});
            skLineSegment(sketch, "E328", {"start": v(7.7, 4.56) * mm, "end": v(7.7, 4.72) * mm});
            skLineSegment(sketch, "E329", {"start": v(7.7, 4.72) * mm, "end": v(7.57, 5.2) * mm});
            skLineSegment(sketch, "E330", {"start": v(7.57, 5.2) * mm, "end": v(7.22, 5.72) * mm});
            skLineSegment(sketch, "E331", {"start": v(7.22, 5.72) * mm, "end": v(6.7, 6.08) * mm});
            skLineSegment(sketch, "E332", {"start": v(6.7, 6.08) * mm, "end": v(6.22, 6.2) * mm});
            skLineSegment(sketch, "E333", {"start": v(6.22, 6.2) * mm, "end": v(6.06, 6.2) * mm});
            skLineSegment(sketch, "E334", {"start": v(6.06, 6.2) * mm, "end": v(5.9, 6.2) * mm});
            skLineSegment(sketch, "E335", {"start": v(5.9, 6.2) * mm, "end": v(5.42, 6.08) * mm});
            skLineSegment(sketch, "E336", {"start": v(5.42, 6.08) * mm, "end": v(4.9, 5.72) * mm});
            skLineSegment(sketch, "E337", {"start": v(4.9, 5.72) * mm, "end": v(4.55, 5.2) * mm});
            skLineSegment(sketch, "E338", {"start": v(4.55, 5.2) * mm, "end": v(4.42, 4.72) * mm});
            skLineSegment(sketch, "E339", {"start": v(4.42, 4.72) * mm, "end": v(4.42, 4.56) * mm});
            skLineSegment(sketch, "E340", {"start": v(4.42, 4.56) * mm, "end": v(4.42, 4.4) * mm});
            skLineSegment(sketch, "E341", {"start": v(4.42, 4.4) * mm, "end": v(4.55, 3.93) * mm});
            skLineSegment(sketch, "E342", {"start": v(4.55, 3.93) * mm, "end": v(4.9, 3.4) * mm});
            skLineSegment(sketch, "E343", {"start": v(4.9, 3.4) * mm, "end": v(5.42, 3.05) * mm});
            skLineSegment(sketch, "E344", {"start": v(5.42, 3.05) * mm, "end": v(5.9, 2.92) * mm});
            skLineSegment(sketch, "E345", {"start": v(5.9, 2.92) * mm, "end": v(6.06, 2.92) * mm});
            skSolve(sketch);
        }
        {
            var Q0;
            Q0=makeQuery(id+"F2.imprint","IMPRINT",FACE,{"disambiguationData":[TD([[makeQuery(id+"F2.imprint","IMPRINT",EDGE,{"derivedFrom":sQuery(id+"F2.wireOp",EDGE,"E2")}),-1.0]])]});
            var Q1;
            Q1=makeQuery(id+"F2.imprint","IMPRINT",FACE,{"disambiguationData":[TD([[makeQuery(id+"F2.imprint","IMPRINT",EDGE,{"derivedFrom":sQuery(id+"F2.wireOp",EDGE,"E298")}),1.0]])]});
            var Q2;
            Q2=makeQuery(id+"F2.imprint","IMPRINT",FACE,{"disambiguationData":[TD([[makeQuery(id+"F2.imprint","IMPRINT",EDGE,{"derivedFrom":sQuery(id+"F2.wireOp",EDGE,"E322")}),1.0]])]});
            extrude(context, id + "F3", {"entities" : qUnion([Q0, Q1, Q2]), "operationType" : NewBodyOperationType.REMOVE, "oppositeDirection" : true, "depth" : 1 * mm});
        }
        {
            var Q0;
            Q0=makeQuery(id+"F3.boolean.opBoolean","SPLIT",FACE,{"disambiguationData":[TD([makeQuery(id+"F3.opExtrude","SWEPT_FACE",FACE,{"disambiguationData":[OSD([sQuery(id+"F2.wireOp",EDGE,"E205")])]})])],"derivedFrom":makeQuery(id+"F1.opExtrude","CAP_FACE",FACE,{"disambiguationData":[OSD([sQuery(id+"F0.wireOp",EDGE,"E0.bottom"),sQuery(id+"F0.wireOp",EDGE,"E0.top"),sQuery(id+"F0.wireOp",EDGE,"E0.left"),sQuery(id+"F0.wireOp",EDGE,"E0.right")])],"isStart":false})});
            var Q1;
            Q1=makeQuery(id+"F3.boolean.opBoolean","SPLIT",FACE,{"disambiguationData":[TD([makeQuery(id+"F3.opExtrude","SWEPT_FACE",FACE,{"disambiguationData":[OSD([sQuery(id+"F2.wireOp",EDGE,"E274")])]})])],"derivedFrom":makeQuery(id+"F1.opExtrude","CAP_FACE",FACE,{"disambiguationData":[OSD([sQuery(id+"F0.wireOp",EDGE,"E0.bottom"),sQuery(id+"F0.wireOp",EDGE,"E0.top"),sQuery(id+"F0.wireOp",EDGE,"E0.left"),sQuery(id+"F0.wireOp",EDGE,"E0.right")])],"isStart":false})});
            extrude(context, id + "F4", {"entities" : qUnion([Q0, Q1]), "operationType" : NewBodyOperationType.REMOVE, "oppositeDirection" : true, "depth" : .5 * mm});
        }
        {
            var Q0;
            Q0=makeQuery(id+"F3.boolean.opBoolean","COPY",EDGE,{"derivedFrom":makeQuery(id+"F3.opExtrude","SWEPT_EDGE",EDGE,{"disambiguationData":[OSD([sQuery(id+"F2.wireOp",EDGE,"E171"),sQuery(id+"F2.wireOp",EDGE,"E172")])]})});
            var Q1;
            Q1=makeQuery(id+"F3.boolean.opBoolean","COPY",EDGE,{"derivedFrom":makeQuery(id+"F3.opExtrude","SWEPT_EDGE",EDGE,{"disambiguationData":[OSD([sQuery(id+"F2.wireOp",EDGE,"E172"),sQuery(id+"F2.wireOp",EDGE,"E173")])]})});
            var Q2;
            Q2=makeQuery(id+"F3.boolean.opBoolean","COPY",EDGE,{"derivedFrom":makeQuery(id+"F3.opExtrude","SWEPT_EDGE",EDGE,{"disambiguationData":[OSD([sQuery(id+"F2.wireOp",EDGE,"E173"),sQuery(id+"F2.wireOp",EDGE,"E174")])]})});
            var Q3;
            Q3=makeQuery(id+"F3.boolean.opBoolean","COPY",EDGE,{"derivedFrom":makeQuery(id+"F3.opExtrude","SWEPT_EDGE",EDGE,{"disambiguationData":[OSD([sQuery(id+"F2.wireOp",EDGE,"E170"),sQuery(id+"F2.wireOp",EDGE,"E171")])]})});
            var Q4;
            Q4=makeQuery(id+"F3.boolean.opBoolean","COPY",EDGE,{"derivedFrom":makeQuery(id+"F3.opExtrude","SWEPT_EDGE",EDGE,{"disambiguationData":[OSD([sQuery(id+"F2.wireOp",EDGE,"E174"),sQuery(id+"F2.wireOp",EDGE,"E175")])]})});
            var Q5;
            Q5=makeQuery(id+"F3.boolean.opBoolean","COPY",EDGE,{"derivedFrom":makeQuery(id+"F3.opExtrude","SWEPT_EDGE",EDGE,{"disambiguationData":[OSD([sQuery(id+"F2.wireOp",EDGE,"E175"),sQuery(id+"F2.wireOp",EDGE,"E176")])]})});
            var Q6;
            Q6=makeQuery(id+"F3.boolean.opBoolean","COPY",EDGE,{"derivedFrom":makeQuery(id+"F3.opExtrude","SWEPT_EDGE",EDGE,{"disambiguationData":[OSD([sQuery(id+"F2.wireOp",EDGE,"E169"),sQuery(id+"F2.wireOp",EDGE,"E170")])]})});
            var Q7;
            Q7=makeQuery(id+"F3.boolean.opBoolean","COPY",EDGE,{"derivedFrom":makeQuery(id+"F3.opExtrude","SWEPT_EDGE",EDGE,{"disambiguationData":[OSD([sQuery(id+"F2.wireOp",EDGE,"E168"),sQuery(id+"F2.wireOp",EDGE,"E169")])]})});
            var Q8;
            Q8=makeQuery(id+"F3.boolean.opBoolean","COPY",EDGE,{"derivedFrom":makeQuery(id+"F3.opExtrude","SWEPT_EDGE",EDGE,{"disambiguationData":[OSD([sQuery(id+"F2.wireOp",EDGE,"E167"),sQuery(id+"F2.wireOp",EDGE,"E168")])]})});
            var Q9;
            Q9=makeQuery(id+"F3.boolean.opBoolean","COPY",EDGE,{"derivedFrom":makeQuery(id+"F3.opExtrude","SWEPT_EDGE",EDGE,{"disambiguationData":[OSD([sQuery(id+"F2.wireOp",EDGE,"E176"),sQuery(id+"F2.wireOp",EDGE,"E177")])]})});
            var Q10;
            Q10=makeQuery(id+"F3.boolean.opBoolean","COPY",EDGE,{"derivedFrom":makeQuery(id+"F3.opExtrude","SWEPT_EDGE",EDGE,{"disambiguationData":[OSD([sQuery(id+"F2.wireOp",EDGE,"E177"),sQuery(id+"F2.wireOp",EDGE,"E178")])]})});
            var Q11;
            Q11=makeQuery(id+"F3.boolean.opBoolean","COPY",EDGE,{"derivedFrom":makeQuery(id+"F3.opExtrude","SWEPT_EDGE",EDGE,{"disambiguationData":[OSD([sQuery(id+"F2.wireOp",EDGE,"E251"),sQuery(id+"F2.wireOp",EDGE,"E252")])]})});
            var Q12;
            Q12=makeQuery(id+"F3.boolean.opBoolean","COPY",EDGE,{"derivedFrom":makeQuery(id+"F3.opExtrude","SWEPT_EDGE",EDGE,{"disambiguationData":[OSD([sQuery(id+"F2.wireOp",EDGE,"E229"),sQuery(id+"F2.wireOp",EDGE,"E230")])]})});
            var Q13;
            Q13=makeQuery(id+"F3.boolean.opBoolean","COPY",EDGE,{"derivedFrom":makeQuery(id+"F3.opExtrude","SWEPT_EDGE",EDGE,{"disambiguationData":[OSD([sQuery(id+"F2.wireOp",EDGE,"E244"),sQuery(id+"F2.wireOp",EDGE,"E245")])]})});
            var Q14;
            Q14=makeQuery(id+"F3.boolean.opBoolean","COPY",EDGE,{"derivedFrom":makeQuery(id+"F3.opExtrude","SWEPT_EDGE",EDGE,{"disambiguationData":[OSD([sQuery(id+"F2.wireOp",EDGE,"E245"),sQuery(id+"F2.wireOp",EDGE,"E246")])]})});
            var Q15;
            Q15=makeQuery(id+"F3.boolean.opBoolean","COPY",EDGE,{"derivedFrom":makeQuery(id+"F3.opExtrude","SWEPT_EDGE",EDGE,{"disambiguationData":[OSD([sQuery(id+"F2.wireOp",EDGE,"E246"),sQuery(id+"F2.wireOp",EDGE,"E247")])]})});
            var Q16;
            Q16=makeQuery(id+"F3.boolean.opBoolean","COPY",EDGE,{"derivedFrom":makeQuery(id+"F3.opExtrude","SWEPT_EDGE",EDGE,{"disambiguationData":[OSD([sQuery(id+"F2.wireOp",EDGE,"E236"),sQuery(id+"F2.wireOp",EDGE,"E237")])]})});
            var Q17;
            Q17=makeQuery(id+"F3.boolean.opBoolean","COPY",EDGE,{"derivedFrom":makeQuery(id+"F3.opExtrude","SWEPT_EDGE",EDGE,{"disambiguationData":[OSD([sQuery(id+"F2.wireOp",EDGE,"E235"),sQuery(id+"F2.wireOp",EDGE,"E236")])]})});
            var Q18;
            Q18=makeQuery(id+"F3.boolean.opBoolean","COPY",EDGE,{"derivedFrom":makeQuery(id+"F3.opExtrude","SWEPT_EDGE",EDGE,{"disambiguationData":[OSD([sQuery(id+"F2.wireOp",EDGE,"E234"),sQuery(id+"F2.wireOp",EDGE,"E235")])]})});
            var Q19;
            Q19=makeQuery(id+"F3.boolean.opBoolean","COPY",EDGE,{"derivedFrom":makeQuery(id+"F3.opExtrude","SWEPT_EDGE",EDGE,{"disambiguationData":[OSD([sQuery(id+"F2.wireOp",EDGE,"E247"),sQuery(id+"F2.wireOp",EDGE,"E248")])]})});
            var Q20;
            Q20=makeQuery(id+"F3.boolean.opBoolean","COPY",EDGE,{"derivedFrom":makeQuery(id+"F3.opExtrude","SWEPT_EDGE",EDGE,{"disambiguationData":[OSD([sQuery(id+"F2.wireOp",EDGE,"E233"),sQuery(id+"F2.wireOp",EDGE,"E234")])]})});
            var Q21;
            Q21=makeQuery(id+"F3.boolean.opBoolean","COPY",EDGE,{"derivedFrom":makeQuery(id+"F3.opExtrude","SWEPT_EDGE",EDGE,{"disambiguationData":[OSD([sQuery(id+"F2.wireOp",EDGE,"E276"),sQuery(id+"F2.wireOp",EDGE,"E277")])]})});
            var Q22;
            Q22=makeQuery(id+"F3.boolean.opBoolean","COPY",EDGE,{"derivedFrom":makeQuery(id+"F3.opExtrude","SWEPT_EDGE",EDGE,{"disambiguationData":[OSD([sQuery(id+"F2.wireOp",EDGE,"E278"),sQuery(id+"F2.wireOp",EDGE,"E279")])]})});
            var Q23;
            Q23=makeQuery(id+"F3.boolean.opBoolean","COPY",EDGE,{"derivedFrom":makeQuery(id+"F3.opExtrude","SWEPT_EDGE",EDGE,{"disambiguationData":[OSD([sQuery(id+"F2.wireOp",EDGE,"E279"),sQuery(id+"F2.wireOp",EDGE,"E280")])]})});
            var Q24;
            Q24=makeQuery(id+"F3.boolean.opBoolean","COPY",EDGE,{"derivedFrom":makeQuery(id+"F3.opExtrude","SWEPT_EDGE",EDGE,{"disambiguationData":[OSD([sQuery(id+"F2.wireOp",EDGE,"E275"),sQuery(id+"F2.wireOp",EDGE,"E276")])]})});
            var Q25;
            Q25=makeQuery(id+"F3.boolean.opBoolean","COPY",EDGE,{"derivedFrom":makeQuery(id+"F3.opExtrude","SWEPT_EDGE",EDGE,{"disambiguationData":[OSD([sQuery(id+"F2.wireOp",EDGE,"E257"),sQuery(id+"F2.wireOp",EDGE,"E258")])]})});
            var Q26;
            Q26=makeQuery(id+"F3.boolean.opBoolean","COPY",EDGE,{"derivedFrom":makeQuery(id+"F3.opExtrude","SWEPT_EDGE",EDGE,{"disambiguationData":[OSD([sQuery(id+"F2.wireOp",EDGE,"E256"),sQuery(id+"F2.wireOp",EDGE,"E257")])]})});
            var Q27;
            Q27=makeQuery(id+"F3.boolean.opBoolean","COPY",EDGE,{"derivedFrom":makeQuery(id+"F3.opExtrude","SWEPT_EDGE",EDGE,{"disambiguationData":[OSD([sQuery(id+"F2.wireOp",EDGE,"E223"),sQuery(id+"F2.wireOp",EDGE,"E224")])]})});
            var Q28;
            Q28=makeQuery(id+"F3.boolean.opBoolean","COPY",EDGE,{"derivedFrom":makeQuery(id+"F3.opExtrude","SWEPT_EDGE",EDGE,{"disambiguationData":[OSD([sQuery(id+"F2.wireOp",EDGE,"E224"),sQuery(id+"F2.wireOp",EDGE,"E225")])]})});
            fillet(context, id + "F5", {"entities" : qUnion([Q0, Q1, Q2, Q3, Q4, Q5, Q6, Q7, Q8, Q9, Q10, Q11, Q12, Q13, Q14, Q15, Q16, Q17, Q18, Q19, Q20, Q21, Q22, Q23, Q24, Q25, Q26, Q27, Q28]), "radius" : 5 * mm, "tangentPropagation" : true, "allowEdgeOverflow" : false});
        }
    });
